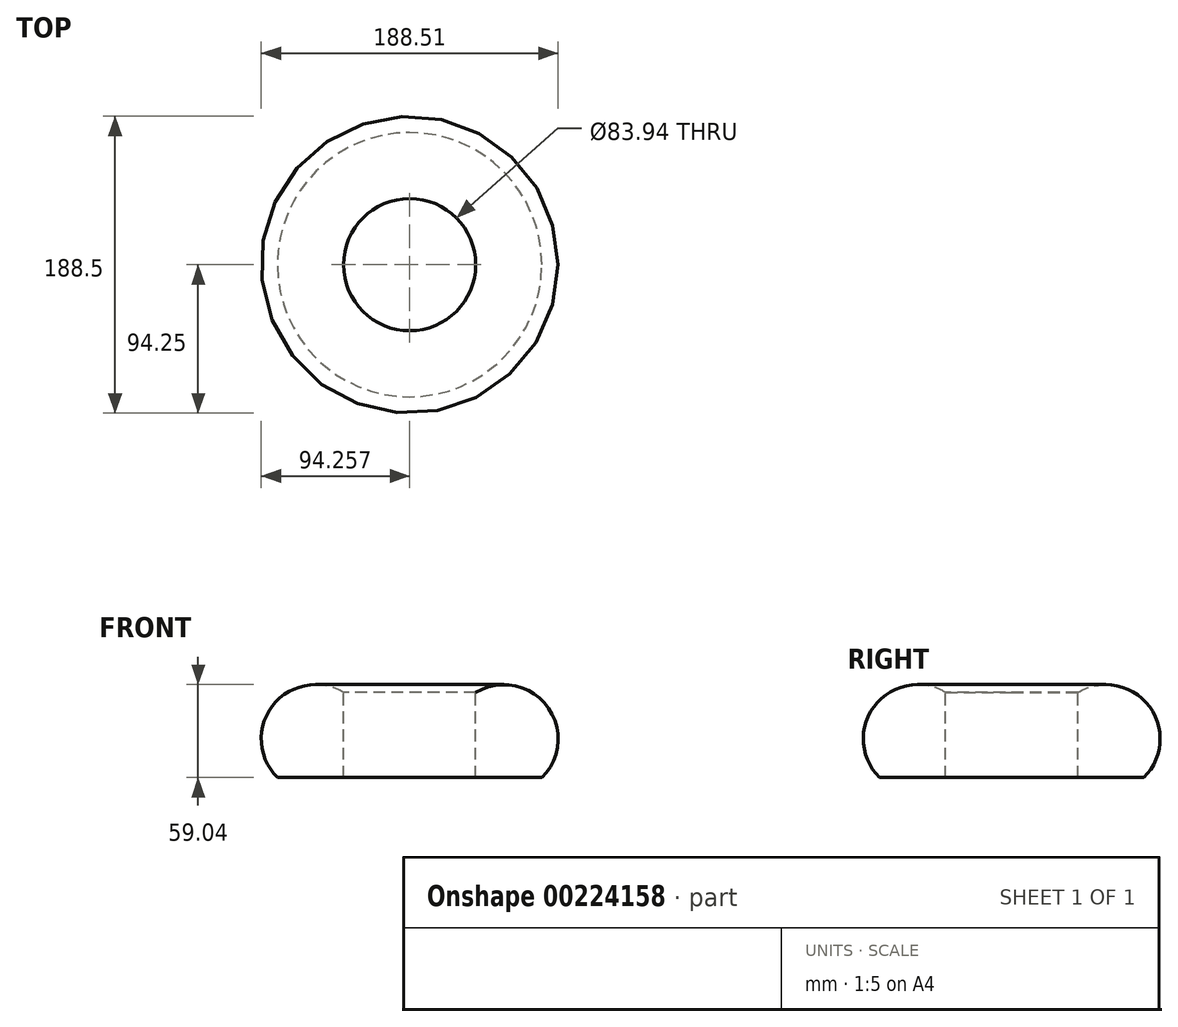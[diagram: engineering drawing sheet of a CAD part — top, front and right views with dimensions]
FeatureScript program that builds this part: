
annotation { "Feature Type Name" : "Feature", "Feature Type Description" : "" }
export const myFeature = defineFeature(function(context is Context, id is Id, definition is map)
    precondition{}
    {
        {
            var Q0;
            Q0=qCreatedBy(makeId("Front.planeOp"),FACE);
            var sketch = newSketch(context, id + "F0", { "sketchPlane" : qUnion([Q0])});
            skLineSegment(sketch, "E0", {"start": v(0, 54.07) * mm, "end": v(0, 0) * mm});
            skLineSegment(sketch, "E1", {"start": v(0, 0) * mm, "end": v(41.97, 0) * mm});
            skArc(sketch, "E2", {"start": v(41.97, 0) * mm, "mid": v(45.04, 45.7) * mm, "end": v(0, 54.07) * mm});
            skLineSegment(sketch, "E3", {"start": v(-41.97, 59.9) * mm, "end": v(-41.97, -21.71) * mm});
            skSolve(sketch);
        }
        {
            var Q0;
            Q0=makeQuery(id+"F0.imprint","IMPRINT",FACE,{"disambiguationData":[TD([[makeQuery(id+"F0.imprint","IMPRINT",EDGE,{"derivedFrom":sQuery(id+"F0.wireOp",EDGE,"E0")}),1.0]])]});
            var Q1;
            Q1=sQuery(id+"F0.wireOp",EDGE,"E3");
            revolve(context, id + "F1", {"entities" : qUnion([Q0]), "axis" : qUnion([Q1]), "revolveType" : RevolveType.FULL});
        }
    });
